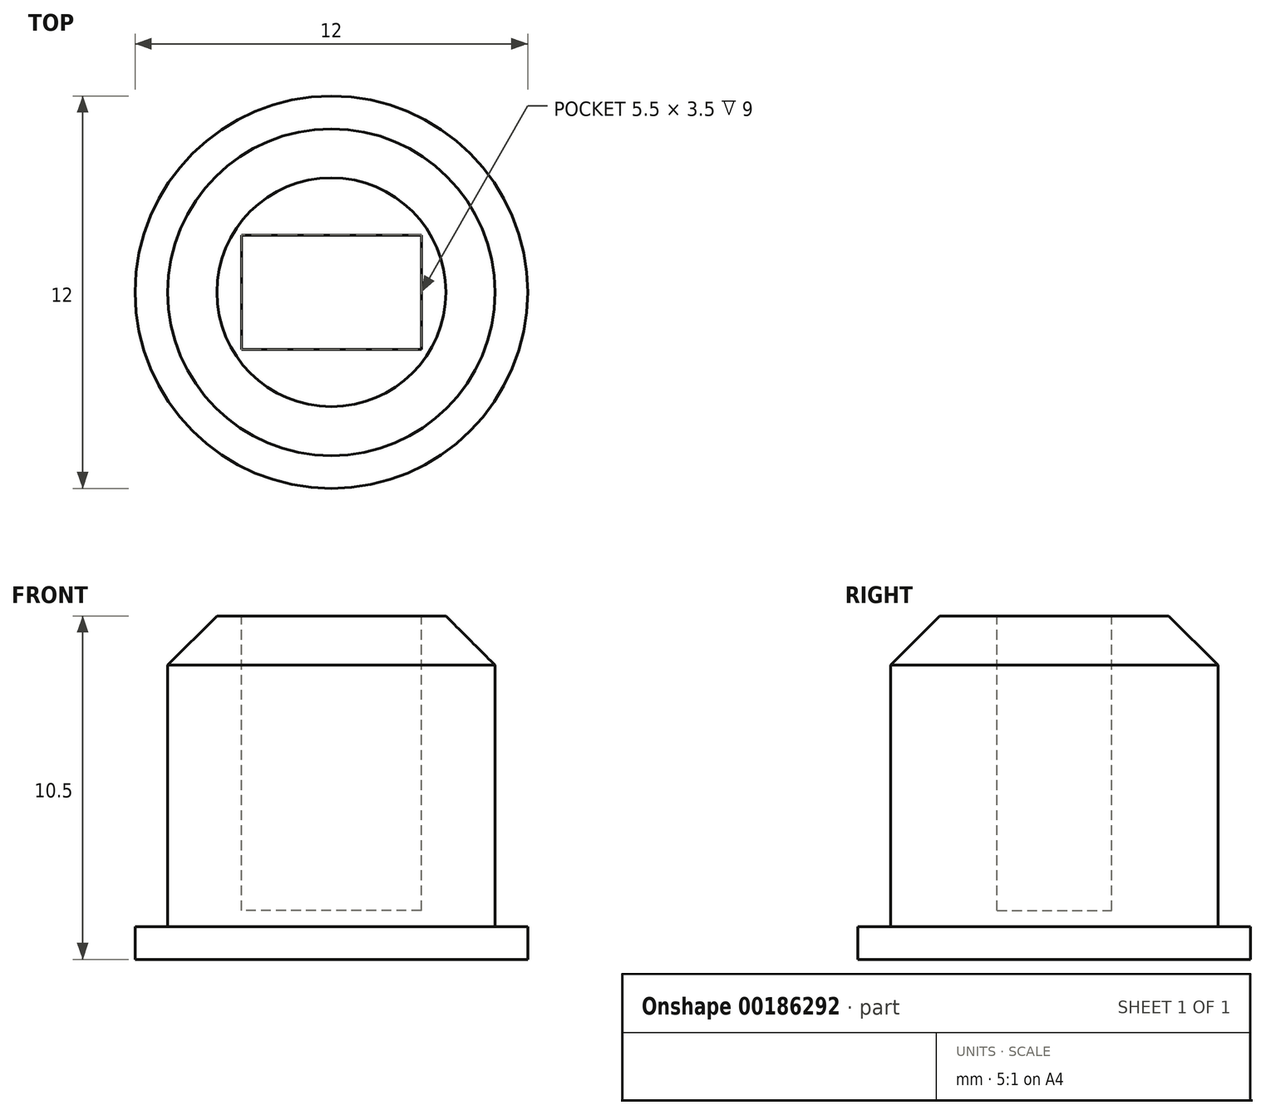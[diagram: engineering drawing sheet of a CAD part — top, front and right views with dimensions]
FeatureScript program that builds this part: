
annotation { "Feature Type Name" : "Feature", "Feature Type Description" : "" }
export const myFeature = defineFeature(function(context is Context, id is Id, definition is map)
    precondition{}
    {
        {
            var Q0;
            Q0=qCreatedBy(makeId("Top.planeOp"),FACE);
            var sketch = newSketch(context, id + "F0", { "sketchPlane" : qUnion([Q0])});
            skCircle(sketch, "E0", {"center": v(0, 0) * mm, "radius": 5 * mm});
            skSolve(sketch);
        }
        {
            var Q0;
            Q0=makeQuery(id+"F0.imprint","IMPRINT",FACE,{"disambiguationData":[TD([[makeQuery(id+"F0.imprint","IMPRINT",EDGE,{"derivedFrom":sQuery(id+"F0.wireOp",EDGE,"E0")}),1.0]])]});
            extrude(context, id + "F1", {"entities" : qUnion([Q0]), "offsetDistance" : 25 * mm, "depth" : 9.5 * mm});
        }
        {
            var Q0;
            Q0=makeQuery(id+"F1.opExtrude","CAP_EDGE",EDGE,{"disambiguationData":[OSD([sQuery(id+"F0.wireOp",EDGE,"E0")])],"isStart":false});
            chamfer(context, id + "F2", {"entities" : qUnion([Q0]), "width" : 1.5 * mm, "tangentPropagation" : true});
        }
        {
            var Q0;
            Q0=makeQuery(id+"F1.opExtrude","CAP_FACE",FACE,{"disambiguationData":[OSD([sQuery(id+"F0.wireOp",EDGE,"E0")])],"isStart":false});
            var sketch = newSketch(context, id + "F3", { "sketchPlane" : qUnion([Q0])});
            skLineSegment(sketch, "E1.bottom", {"start": v(2.75, -1.75) * mm, "end": v(-2.75, -1.75) * mm});
            skLineSegment(sketch, "E1.top", {"start": v(2.75, 1.75) * mm, "end": v(-2.75, 1.75) * mm});
            skLineSegment(sketch, "E1.left", {"start": v(2.75, -1.75) * mm, "end": v(2.75, 1.75) * mm});
            skLineSegment(sketch, "E1.right", {"start": v(-2.75, -1.75) * mm, "end": v(-2.75, 1.75) * mm});
            skPoint(sketch, "E1.middle", {"position": v(0, 0) * mm});
            skSolve(sketch);
        }
        {
            var Q0;
            Q0=makeQuery(id+"F0.imprint","IMPRINT",FACE,{"disambiguationData":[TD([[makeQuery(id+"F0.imprint","IMPRINT",EDGE,{"derivedFrom":sQuery(id+"F0.wireOp",EDGE,"E0")}),1.0]])]});
            var sketch = newSketch(context, id + "F4", { "sketchPlane" : qUnion([Q0])});
            skCircle(sketch, "E2", {"center": v(0, 0) * mm, "radius": 6 * mm});
            skSolve(sketch);
        }
        {
            var Q0;
            Q0 = qSketchRegion(id + "F4", true);
            extrude(context, id + "F5", {"entities" : qUnion([Q0]), "operationType" : NewBodyOperationType.ADD, "oppositeDirection" : true, "depth" : 1 * mm, "offsetDistance" : 25 * mm});
        }
        {
            var Q0;
            Q0=makeQuery(id+"F3.imprint","IMPRINT",FACE,{"disambiguationData":[TD([[makeQuery(id+"F3.imprint","IMPRINT",EDGE,{"derivedFrom":sQuery(id+"F3.wireOp",EDGE,"E1.bottom")}),-1.0]])]});
            extrude(context, id + "F6", {"entities" : qUnion([Q0]), "operationType" : NewBodyOperationType.REMOVE, "oppositeDirection" : true, "depth" : 9 * mm, "offsetDistance" : 25 * mm});
        }
    });
